# Revit family: Toilet_Seat-Commercial-American_Standard-Heavy_Duty-59011X0_Series
name_source: partatom
category: Specialty Equipment
revit_build: Autodesk Revit 2018 (Build: 20170223_1515(x64)
units: mm (PartAtom-declared; Revit-internal decimal feet)

## family parameters
Always vertical = No
Cut with Voids When Loaded = No
OmniClass Number = 23.40.20.21
OmniClass Title = Toilet and Bath Specialties
Part Type = Normal
Room Calculation Point = No
Round Connector Dimension = Use Diameter
Shared = Yes
Work Plane-Based = Yes

## types (3) — shared parameters
Assembly Code = C1030200
Default Elevation = 0"
Finish = Plastic-American Standard-020-White
Height = 1"
Installation Type = Surface Mounted
Length = 18 9/16"
Manufacturer = American Standard
Material = Plastic-American Standard-020-White
Price = Prices may vary. Please consult Manufacturer Representative for most up-to-date price list.
Product Documentation Link = https://americanstandard.box.com
Product Page URL = https://www.americanstandard-us.com
Revised Date = 01/30/2020
URL = http://www.americanstandard-us.com
Warranty Information = 1 Year Limited Warranty
Width = 14 3/8"

## per-type parameters (varying)
| type | Description |
| 5901.100.020 | Commercial Heavy Duty Open Front Elongated Toilet Seat |
| 5901.100SS.020 | Commercial Heavy Duty Open Front Elongated Toilet Seat with EverClean® Surface and Self-sustaining Hinges |
| 5901.110T.020 | Commercial Heavy Duty Open Front Elongated Toilet Seat Wth EverClean® Surface |

note: column(s) folded — value = type name in every type: Model

## geometry (parser evidence)
native form markers: Sweep x2
no freeform markers — native parametric forms only
